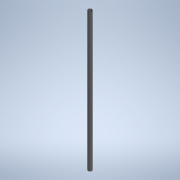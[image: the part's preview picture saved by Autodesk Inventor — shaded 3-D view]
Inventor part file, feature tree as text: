
AUTODESK INVENTOR PART (.ipt)
format: ipt  version: 2020 (Build 240168000, 168)  size: 96,256 bytes
history: native  units: mm
features: extrude x1, sketch x1
ambient origin geometry x8: Origin, YZ Plane, XZ Plane, XY Plane, X Axis, Y Axis, Z Axis, Center Point
bodies: Solid1 (feature_tree)
feature tree (2):
  extrude  "Extrusion1"  Depth=900.0mm
  sketch  "Sketch1"  dims[d0=25.0mm d1=21.0mm d2=900.0mm d3=0.0mm d4=0.5mm d5=0.872665mm d6=0.5mm d7=0.872665mm]
